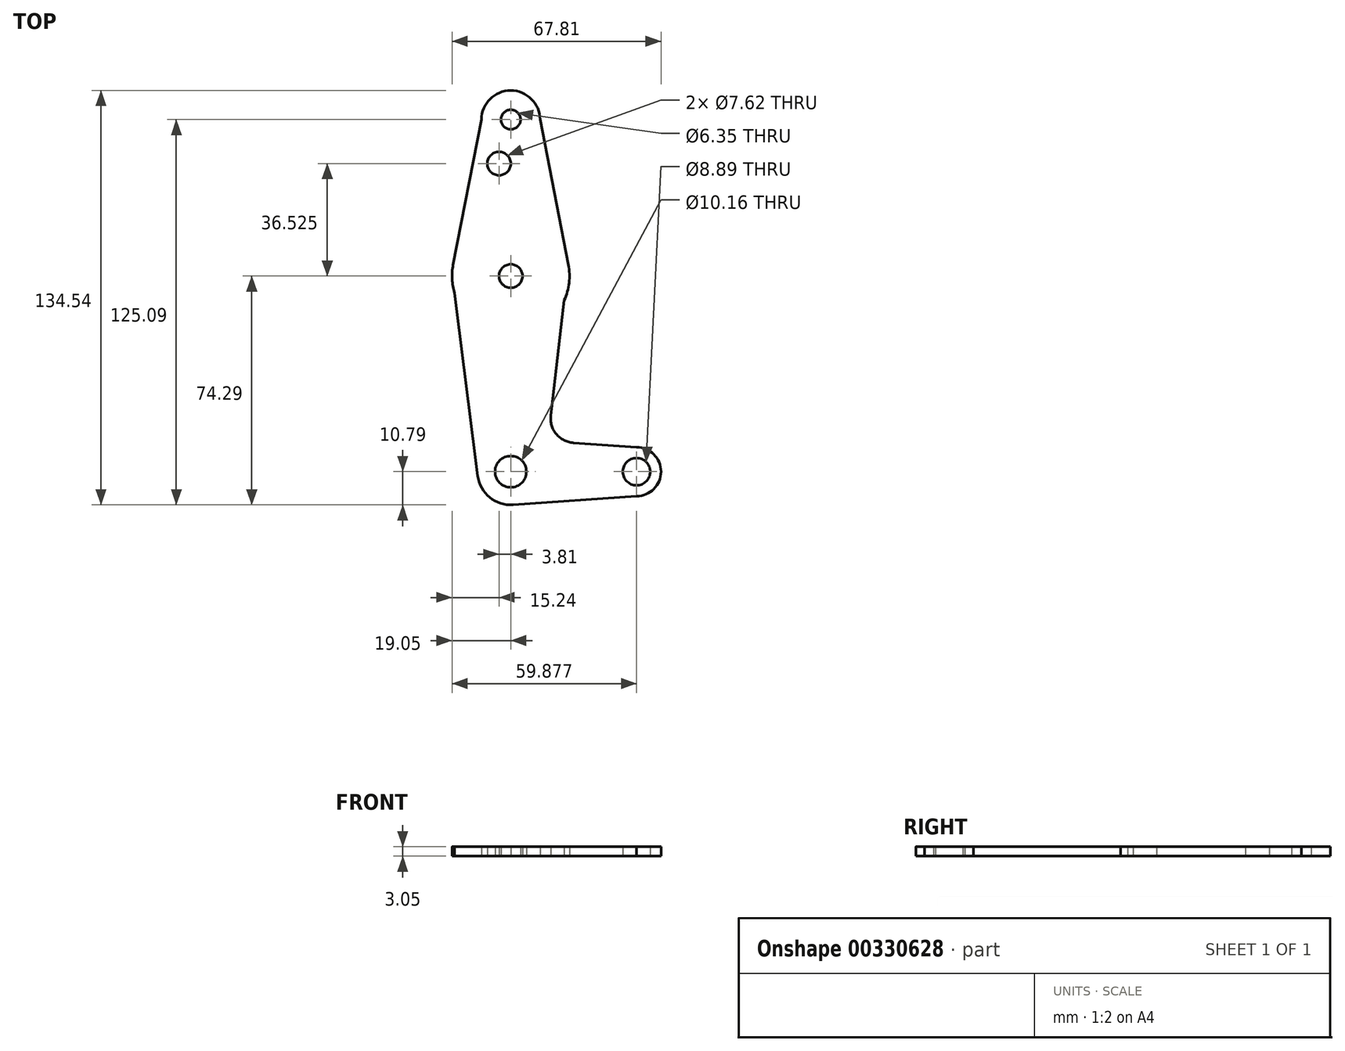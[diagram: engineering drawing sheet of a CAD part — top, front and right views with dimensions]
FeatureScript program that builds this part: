
annotation { "Feature Type Name" : "Feature", "Feature Type Description" : "" }
export const myFeature = defineFeature(function(context is Context, id is Id, definition is map)
    precondition{}
    {
        {
            var Q0;
            Q0=qCreatedBy(makeId("Top.planeOp"),FACE);
            var sketch = newSketch(context, id + "F0", { "sketchPlane" : qUnion([Q0])});
            skLineSegment(sketch, "E0", {"start": v(0, 0) * mm, "end": v(0, 114.3) * mm});
            skLineSegment(sketch, "E1", {"start": v(0, 0) * mm, "end": v(40.83, 0) * mm});
            skCircle(sketch, "E2", {"center": v(40.83, 0) * mm, "radius": 7.94 * mm});
            skCircle(sketch, "E3", {"center": v(0, 0) * mm, "radius": 10.8 * mm});
            skLineSegment(sketch, "E4", {"start": v(0, 114.23) * mm, "end": v(0, 114.3) * mm});
            skCircle(sketch, "E5", {"center": v(0, 114.23) * mm, "radius": 9.53 * mm});
            skCircle(sketch, "E6", {"center": v(0, 63.5) * mm, "radius": 19.05 * mm});
            skLineSegment(sketch, "E7", {"start": v(9.52, 114.3) * mm, "end": v(18.7, 67.14) * mm});
            skLineSegment(sketch, "E8", {"start": v(18.7, 67.14) * mm, "end": v(13, 18.22) * mm});
            skLineSegment(sketch, "E9", {"start": v(-9.52, 114.3) * mm, "end": v(-18.7, 67.14) * mm});
            skLineSegment(sketch, "E10", {"start": v(-19.55, 68.37) * mm, "end": v(-10.7, -1.36) * mm});
            skLineSegment(sketch, "E11", {"start": v(40.83, -7.94) * mm, "end": v(0, -10.82) * mm});
            skLineSegment(sketch, "E12", {"start": v(20.34, 9.37) * mm, "end": v(40.83, 7.94) * mm});
            skCircle(sketch, "E13", {"center": v(0, 114.3) * mm, "radius": 3.18 * mm});
            skArc(sketch, "E14.filletArc", {"start": v(13, 18.22) * mm, "mid": v(14.77, 12.23) * mm, "end": v(20.34, 9.37) * mm});
            skCircle(sketch, "E15", {"center": v(0, 63.5) * mm, "radius": 3.81 * mm});
            skCircle(sketch, "E16", {"center": v(0, 0) * mm, "radius": 5.08 * mm});
            skCircle(sketch, "E17", {"center": v(40.83, 0) * mm, "radius": 4.45 * mm});
            skCircle(sketch, "E18", {"center": v(-3.81, 100.03) * mm, "radius": 3.81 * mm});
            skSolve(sketch);
        }
        {
            var Q0;
            Q0 = qSketchRegion(id + "F0", true);
            extrude(context, id + "F1", {"entities" : qUnion([Q0]), "depth" : 3.05 * mm});
        }
        {
            var Q0;
            {var subQ0=sQuery(id+"F0.wireOp",EDGE,"E16");var subQ1=sQuery(id+"F0.wireOp",EDGE,"E0");var subQ2=makeQuery(id+"F0.imprint","INTERSECT",VERTEX,{"derivedFrom":[subQ1,subQ0]});Q0=makeQuery(id+"F0.imprint","IMPRINT",FACE,{"disambiguationData":[TD([[makeQuery(id+"F0.imprint","IMPRINT",EDGE,{"disambiguationData":[TD([[subQ2,-1.0]])],"derivedFrom":subQ1}),-1.0]])]});}
            extrude(context, id + "F2", {"entities" : qUnion([Q0]), "operationType" : NewBodyOperationType.ADD, "depth" : 3.05 * mm});
        }
    });
